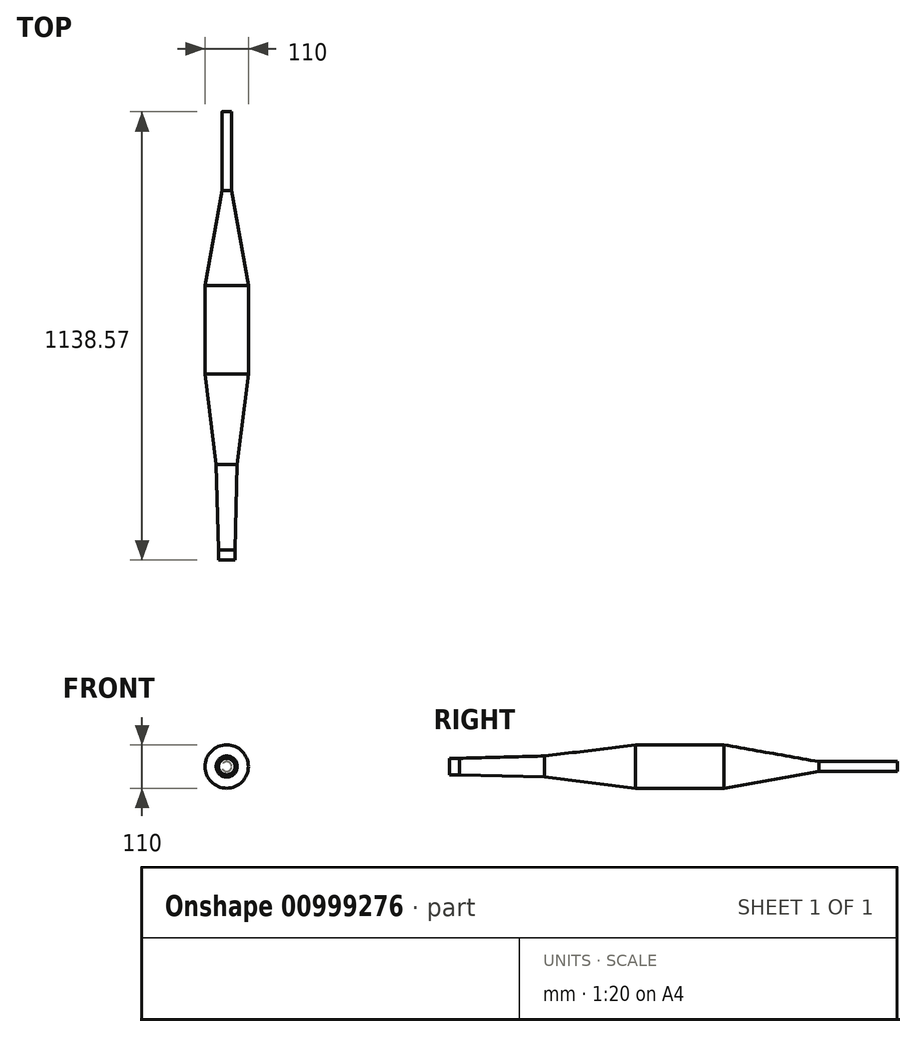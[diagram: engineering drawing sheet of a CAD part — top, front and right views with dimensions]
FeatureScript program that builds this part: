
annotation { "Feature Type Name" : "Feature", "Feature Type Description" : "" }
export const myFeature = defineFeature(function(context is Context, id is Id, definition is map)
    precondition{}
    {
        {
            var Q0;
            Q0=qCreatedBy(makeId("Right.planeOp"),FACE);
            var sketch = newSketch(context, id + "F0", { "sketchPlane" : qUnion([Q0])});
            skLineSegment(sketch, "E0", {"start": v(21.65, -12.5) * mm, "end": v(42.65, 23.87) * mm});
            skLineSegment(sketch, "E1", {"start": v(0, 191.98) * mm, "end": v(0, 233.98) * mm});
            skLineSegment(sketch, "E2", {"start": v(0, 212.98) * mm, "end": v(242, 212.98) * mm});
            skLineSegment(sketch, "E3", {"start": v(0, 212.98) * mm, "end": v(-65, 212.98) * mm});
            skLineSegment(sketch, "E4", {"start": v(242, 239.66) * mm, "end": v(242, 186.3) * mm});
            skLineSegment(sketch, "E5", {"start": v(25, 233.98) * mm, "end": v(242, 239.66) * mm});
            skLineSegment(sketch, "E6", {"start": v(25, 191.98) * mm, "end": v(242, 186.3) * mm});
            skLineSegment(sketch, "E7", {"start": v(-51.1, 50.44) * mm, "end": v(-51.1, 27.44) * mm});
            skLineSegment(sketch, "E8", {"start": v(-51.1, 38.94) * mm, "end": v(10.5, 18.19) * mm});
            skLineSegment(sketch, "E9", {"start": v(242, 212.98) * mm, "end": v(344.06, 212.98) * mm});
            skLineSegment(sketch, "E10", {"start": v(242, 239.66) * mm, "end": v(344.06, 252.2) * mm});
            skLineSegment(sketch, "E11", {"start": v(242, 186.3) * mm, "end": v(344.06, 173.76) * mm});
            skLineSegment(sketch, "E12", {"start": v(344.06, 252.2) * mm, "end": v(344.06, 173.76) * mm});
            skLineSegment(sketch, "E13", {"start": v(344.06, 212.98) * mm, "end": v(472.63, 212.98) * mm});
            skLineSegment(sketch, "E14", {"start": v(472.63, 157.98) * mm, "end": v(472.63, 267.98) * mm});
            skLineSegment(sketch, "E15", {"start": v(344.06, 252.2) * mm, "end": v(472.63, 267.98) * mm});
            skLineSegment(sketch, "E16", {"start": v(344.06, 173.76) * mm, "end": v(472.63, 157.98) * mm});
            skLineSegment(sketch, "E17", {"start": v(472.63, 212.98) * mm, "end": v(853.5, 212.98) * mm});
            skLineSegment(sketch, "E18", {"start": v(853.5, 212.98) * mm, "end": v(938.57, 212.98) * mm});
            skLineSegment(sketch, "E19", {"start": v(938.57, 200.48) * mm, "end": v(938.57, 225.48) * mm});
            skLineSegment(sketch, "E20", {"start": v(697.54, 267.98) * mm, "end": v(1009.46, 212.98) * mm, "construction": true});
            skLineSegment(sketch, "E21", {"start": v(1009.46, 212.98) * mm, "end": v(697.54, 157.98) * mm, "construction": true});
            skLineSegment(sketch, "E22", {"start": v(472.63, 267.98) * mm, "end": v(697.54, 267.98) * mm});
            skLineSegment(sketch, "E23", {"start": v(472.63, 157.98) * mm, "end": v(697.54, 157.98) * mm});
            skLineSegment(sketch, "E24", {"start": v(853.5, 185.48) * mm, "end": v(853.5, 240.48) * mm});
            skLineSegment(sketch, "E25", {"start": v(697.54, 267.98) * mm, "end": v(697.54, 157.98) * mm});
            skLineSegment(sketch, "E26", {"start": v(938.57, 225.48) * mm, "end": v(1138.57, 225.48) * mm});
            skLineSegment(sketch, "E27", {"start": v(938.57, 200.48) * mm, "end": v(1138.57, 200.48) * mm});
            skLineSegment(sketch, "E28", {"start": v(1138.57, 200.48) * mm, "end": v(1138.57, 225.48) * mm});
            skLineSegment(sketch, "E29", {"start": v(697.54, 267.98) * mm, "end": v(938.57, 225.48) * mm});
            skLineSegment(sketch, "E30", {"start": v(697.54, 157.98) * mm, "end": v(938.57, 200.48) * mm});
            skLineSegment(sketch, "E31", {"start": v(21.65, -12.5) * mm, "end": v(21.65, -190.3) * mm, "construction": true});
            skArc(sketch, "E32", {"start": v(32.15, 5.69) * mm, "mid": v(97.18, -130.66) * mm, "end": v(-6.8, -240.23) * mm, "construction": true});
            skLineSegment(sketch, "E33", {"start": v(-34.52, -109.8) * mm, "end": v(77.31, -182.43) * mm, "construction": true});
            skLineSegment(sketch, "E34", {"start": v(99.7, -196.96) * mm, "end": v(54.93, -167.9) * mm});
            skArc(sketch, "E35", {"start": v(99.7, -196.96) * mm, "mid": v(119.73, -74) * mm, "end": v(42.65, 23.87) * mm});
            skArc(sketch, "E36", {"start": v(54.93, -167.9) * mm, "mid": v(70.55, -83.29) * mm, "end": v(21.65, -12.5) * mm});
            skLineSegment(sketch, "E37", {"start": v(-6.8, -240.23) * mm, "end": v(-132.56, -266.96) * mm, "construction": true});
            skLineSegment(sketch, "E38", {"start": v(1.35, -278.6) * mm, "end": v(-14.95, -201.88) * mm});
            skLineSegment(sketch, "E39", {"start": v(-14.95, -201.88) * mm, "end": v(-144, -213.17) * mm});
            skLineSegment(sketch, "E40", {"start": v(1.35, -278.6) * mm, "end": v(-121.12, -320.76) * mm});
            skLineSegment(sketch, "E41", {"start": v(-144, -213.17) * mm, "end": v(-121.12, -320.76) * mm});
            skLineSegment(sketch, "E42", {"start": v(77.31, -182.43) * mm, "end": v(-6.8, -240.23) * mm, "construction": true});
            skArc(sketch, "E43", {"start": v(-14.95, -201.88) * mm, "mid": v(23.13, -191.34) * mm, "end": v(54.93, -167.9) * mm});
            skArc(sketch, "E44", {"start": v(1.35, -278.6) * mm, "mid": v(57.98, -246.75) * mm, "end": v(99.7, -196.96) * mm});
            skLineSegment(sketch, "E45", {"start": v(-132.56, -266.96) * mm, "end": v(-357.47, -266.96) * mm, "construction": true});
            skLineSegment(sketch, "E46", {"start": v(-368.9, -320.76) * mm, "end": v(-346.03, -213.17) * mm});
            skLineSegment(sketch, "E47", {"start": v(-368.9, -320.76) * mm, "end": v(-132.56, -266.96) * mm, "construction": true});
            skLineSegment(sketch, "E48", {"start": v(-357.47, -266.96) * mm, "end": v(-121.12, -320.76) * mm, "construction": true});
            skLineSegment(sketch, "E49", {"start": v(-346.03, -213.17) * mm, "end": v(-144, -213.17) * mm});
            skLineSegment(sketch, "E50", {"start": v(-121.12, -320.76) * mm, "end": v(-368.9, -320.76) * mm});
            skLineSegment(sketch, "E51", {"start": v(-662.57, -202.11) * mm, "end": v(-346.03, -213.17) * mm, "construction": true});
            skLineSegment(sketch, "E52", {"start": v(-662.57, -202.11) * mm, "end": v(-368.9, -320.76) * mm, "construction": true});
            skLineSegment(sketch, "E53", {"start": v(1009.46, 212.98) * mm, "end": v(697.54, 212.98) * mm, "construction": true});
            skLineSegment(sketch, "E54", {"start": v(-357.47, -266.96) * mm, "end": v(-662.57, -202.11) * mm, "construction": true});
            skLineSegment(sketch, "E55", {"start": v(-595.83, -229.08) * mm, "end": v(-590.63, -204.62) * mm});
            skLineSegment(sketch, "E56", {"start": v(-590.63, -204.62) * mm, "end": v(-786.26, -163.04) * mm});
            skLineSegment(sketch, "E57", {"start": v(-786.26, -163.04) * mm, "end": v(-791.46, -187.5) * mm});
            skLineSegment(sketch, "E58", {"start": v(-791.46, -187.5) * mm, "end": v(-595.83, -229.08) * mm});
            skLineSegment(sketch, "E59", {"start": v(-590.63, -204.62) * mm, "end": v(-346.03, -213.17) * mm});
            skLineSegment(sketch, "E60", {"start": v(-595.83, -229.08) * mm, "end": v(-368.9, -320.76) * mm});
            skLineSegment(sketch, "E61", {"start": v(42.65, 23.87) * mm, "end": v(21, 36.37) * mm});
            skLineSegment(sketch, "E62", {"start": v(21, 36.37) * mm, "end": v(0, 0) * mm});
            skLineSegment(sketch, "E63", {"start": v(0, 0) * mm, "end": v(21.65, -12.5) * mm});
            skLineSegment(sketch, "E64", {"start": v(0, 212.98) * mm, "end": v(25, 212.98) * mm});
            skLineSegment(sketch, "E65", {"start": v(25, 233.98) * mm, "end": v(25, 191.98) * mm});
            skLineSegment(sketch, "E66", {"start": v(0, 233.98) * mm, "end": v(25, 233.98) * mm});
            skLineSegment(sketch, "E67", {"start": v(0, 191.98) * mm, "end": v(25, 191.98) * mm});
            skLineSegment(sketch, "E68", {"start": v(-51.1, 27.44) * mm, "end": v(0, 0) * mm});
            skLineSegment(sketch, "E69", {"start": v(-51.1, 50.44) * mm, "end": v(21, 36.37) * mm});
            skLineSegment(sketch, "E70", {"start": v(10.5, 18.19) * mm, "end": v(32.15, 5.69) * mm});
            skLineSegment(sketch, "E71", {"start": v(938.57, 212.98) * mm, "end": v(1138.57, 212.98) * mm});
            skSolve(sketch);
        }
        {
            var Q0;
            {var subQ2=sQuery(id+"F0.wireOp",EDGE,"E64");Q0=makeQuery(id+"F0.imprint","IMPRINT",FACE,{"disambiguationData":[TD([[makeQuery(id+"F0.imprint","IMPRINT",EDGE,{"derivedFrom":subQ2}),1.0]])]});}
            var Q1;
            {var subQ0=sQuery(id+"F0.wireOp",EDGE,"E2");Q1=makeQuery(id+"F0.imprint","IMPRINT",FACE,{"disambiguationData":[TD([[makeQuery(id+"F0.imprint","IMPRINT",EDGE,{"derivedFrom":subQ0}),1.0]])]});}
            var Q2;
            {var subQ0=sQuery(id+"F0.wireOp",EDGE,"E9");Q2=makeQuery(id+"F0.imprint","IMPRINT",FACE,{"disambiguationData":[TD([[makeQuery(id+"F0.imprint","IMPRINT",EDGE,{"derivedFrom":subQ0}),1.0]])]});}
            var Q3;
            {var subQ0=sQuery(id+"F0.wireOp",EDGE,"E13");Q3=makeQuery(id+"F0.imprint","IMPRINT",FACE,{"disambiguationData":[TD([[makeQuery(id+"F0.imprint","IMPRINT",EDGE,{"derivedFrom":subQ0}),1.0]])]});}
            var Q4;
            {var subQ3=sQuery(id+"F0.wireOp",EDGE,"E22");Q4=makeQuery(id+"F0.imprint","IMPRINT",FACE,{"disambiguationData":[TD([[makeQuery(id+"F0.imprint","IMPRINT",EDGE,{"derivedFrom":subQ3}),-1.0]])]});}
            var Q5;
            {var subQ1=sQuery(id+"F0.wireOp",EDGE,"E17");var subQ3=sQuery(id+"F0.wireOp",EDGE,"E25");var subQ4=makeQuery(id+"F0.imprint","INTERSECT",VERTEX,{"derivedFrom":[subQ1,subQ3]});Q5=makeQuery(id+"F0.imprint","IMPRINT",FACE,{"disambiguationData":[TD([[makeQuery(id+"F0.imprint","IMPRINT",EDGE,{"disambiguationData":[TD([[subQ4,-1.0]])],"derivedFrom":subQ1}),1.0]])]});}
            var Q6;
            {var subQ0=sQuery(id+"F0.wireOp",EDGE,"E18");Q6=makeQuery(id+"F0.imprint","IMPRINT",FACE,{"disambiguationData":[TD([[makeQuery(id+"F0.imprint","IMPRINT",EDGE,{"derivedFrom":subQ0}),1.0]])]});}
            var Q7;
            {var subQ2=sQuery(id+"F0.wireOp",EDGE,"E26");Q7=makeQuery(id+"F0.imprint","IMPRINT",FACE,{"disambiguationData":[TD([[makeQuery(id+"F0.imprint","IMPRINT",EDGE,{"derivedFrom":subQ2}),-1.0]])]});}
            var Q8;
            Q8=sQuery(id+"F0.wireOp",EDGE,"E3");
            revolve(context, id + "F1", {"surfaceOperationType" : NewSurfaceOperationType.NEW, "entities" : qUnion([Q0, Q1, Q2, Q3, Q4, Q5, Q6, Q7]), "axis" : qUnion([Q8]), "revolveType" : RevolveType.FULL});
        }
        {
            var Q0;
            {var subQ0=sQuery(id+"F0.wireOp",EDGE,"E61");Q0=makeQuery(id+"F0.imprint","IMPRINT",FACE,{"disambiguationData":[TD([[makeQuery(id+"F0.imprint","IMPRINT",EDGE,{"derivedFrom":subQ0}),1.0]])]});}
            var Q1;
            Q1=sQuery(id+"F0.wireOp",EDGE,"E61");
            var Q2;
            Q2=sQuery(id+"F0.wireOp",EDGE,"E70");
            revolve(context, id + "F2", {"bodyType" : ToolBodyType.SURFACE, "surfaceOperationType" : NewSurfaceOperationType.NEW, "entities" : qUnion([Q0]), "surfaceEntities" : qUnion([Q1]), "axis" : qUnion([Q2]), "revolveType" : RevolveType.FULL});
        }
        {
            var Q0;
            Q0=sQuery(id+"F0.wireOp",EDGE,"E34");
            var Q1;
            {var subQ0=sQuery(id+"F0.wireOp",EDGE,"E36");Q1=makeQuery(id+"F0.imprint","IMPRINT",FACE,{"disambiguationData":[TD([[makeQuery(id+"F0.imprint","IMPRINT",EDGE,{"derivedFrom":subQ0}),-1.0]])]});}
            cPlane(context, id + "F3", {"entities" : qUnion([Q0, Q1]), "cplaneType" : CPlaneType.LINE_ANGLE, "offset" : 0 * mm, "angle" : 90 * degree, "width" : 152.4 * mm, "height" : 152.4 * mm});
        }
        {
            var Q0;
            Q0=qCreatedBy(id+"F3.planeOp",FACE);
            var sketch = newSketch(context, id + "F4", { "sketchPlane" : qUnion([Q0])});
            skCircle(sketch, "E72", {"center": v(0, -164.2) * mm, "radius": 26.68 * mm});
            skSolve(sketch);
        }
        {
            var Q0;
            Q0=makeQuery(id+"F4.imprint","IMPRINT",FACE,{"disambiguationData":[TD([[makeQuery(id+"F4.imprint","IMPRINT",EDGE,{"derivedFrom":sQuery(id+"F4.wireOp",EDGE,"E72")}),1.0]])]});
            var Q1;
            Q1=makeQuery(id+"F2.opRevolve","SWEPT_BODY",BODY,{"disambiguationData":[OSD([sQuery(id+"F0.wireOp",EDGE,"E61")])]});
            var Q2;
            Q2=makeQuery(id+"F2.opRevolve","SWEPT_EDGE",EDGE,{"disambiguationData":[OSD([sQuery(id+"F0.wireOp",VERTEX,"E61.start")])]});
            var Q3;
            Q3=sQuery(id+"F4.wireOp",EDGE,"E72");
            var Q4;
            Q4=sQuery(id+"F0.wireOp",EDGE,"E35");
            var Q5;
            Q5=sQuery(id+"F0.wireOp",EDGE,"E36");
            loft(context, id + "F5", {"bodyType" : ToolBodyType.SURFACE, "operationType" : NewBodyOperationType.ADD, "surfaceOperationType" : NewSurfaceOperationType.ADD, "addGuides" : true, "sheetProfilesArray" : [{ "sheetProfileEntities" : qUnion([Q0]) }, { "sheetProfileEntities" : qUnion([Q1]) }], "wireProfilesArray" : [{ "wireProfileEntities" : qUnion([Q2]) }, { "wireProfileEntities" : qUnion([Q3]) }], "guidesArray" : [{ "guideEntities" : qUnion([Q4]), "guideDerivativeType" : LoftGuideDerivativeType.DEFAULT, "guideDerivativeMagnitude" : 1 }, { "guideEntities" : qUnion([Q5]), "guideDerivativeType" : LoftGuideDerivativeType.DEFAULT, "guideDerivativeMagnitude" : 1 }]});
        }
        {
            var Q0;
            Q0=sQuery(id+"F0.wireOp",EDGE,"E38");
            var Q1;
            {var subQ5=sQuery(id+"F0.wireOp",EDGE,"E43");Q1=makeQuery(id+"F0.imprint","IMPRINT",FACE,{"disambiguationData":[TD([[makeQuery(id+"F0.imprint","IMPRINT",EDGE,{"derivedFrom":subQ5}),-1.0]])]});}
            cPlane(context, id + "F6", {"entities" : qUnion([Q0, Q1]), "cplaneType" : CPlaneType.LINE_ANGLE, "offset" : 25.4 * mm, "angle" : 93 * degree, "width" : 152.4 * mm, "height" : 152.4 * mm});
        }
        {
            var Q0;
            Q0=qCreatedBy(id+"F6.planeOp",FACE);
            var sketch = newSketch(context, id + "F7", { "sketchPlane" : qUnion([Q0])});
            skCircle(sketch, "E73", {"center": v(-2.96, -233.57) * mm, "radius": 39.21 * mm});
            skSolve(sketch);
        }
        {
            var Q1;
            Q1=makeQuery(id+"F5.opLoft","CAP_FACE",FACE,{"disambiguationData":[OSD([makeQuery(id+"F4.imprint","IMPRINT",FACE,{"disambiguationData":[TD([[makeQuery(id+"F4.imprint","IMPRINT",EDGE,{"derivedFrom":sQuery(id+"F4.wireOp",EDGE,"E72")}),1.0]])]})])],"isStart":true});
            var Q2;
            Q2=makeQuery(id+"F7.imprint","IMPRINT",FACE,{"disambiguationData":[TD([[makeQuery(id+"F7.imprint","IMPRINT",EDGE,{"derivedFrom":sQuery(id+"F7.wireOp",EDGE,"E73")}),1.0]])]});
            var Q3;
            Q3=sQuery(id+"F7.wireOp",EDGE,"E73");
            var Q4;
            Q4=makeQuery(id+"F4.imprint","IMPRINT",FACE,{"disambiguationData":[TD([[makeQuery(id+"F4.imprint","IMPRINT",EDGE,{"derivedFrom":sQuery(id+"F4.wireOp",EDGE,"E72")}),1.0]])]});
            var Q5;
            Q5=sQuery(id+"F0.wireOp",EDGE,"E44");
            var Q6;
            Q6=sQuery(id+"F0.wireOp",EDGE,"E43");
            loft(context, id + "F8", {"bodyType" : ToolBodyType.SURFACE, "operationType" : NewBodyOperationType.ADD, "addGuides" : true, "sheetProfilesArray" : [{ "sheetProfileEntities" : qUnion([Q1]) }, { "sheetProfileEntities" : qUnion([Q2]) }], "wireProfilesArray" : [{ "wireProfileEntities" : qUnion([Q3]) }, { "wireProfileEntities" : qUnion([Q4]) }], "guidesArray" : [{ "guideEntities" : qUnion([Q5]), "guideDerivativeType" : LoftGuideDerivativeType.DEFAULT, "guideDerivativeMagnitude" : 1 }, { "guideEntities" : qUnion([Q6]), "guideDerivativeType" : LoftGuideDerivativeType.DEFAULT, "guideDerivativeMagnitude" : 1 }]});
        }
        {
            var Q0;
            Q0=sQuery(id+"F0.wireOp",EDGE,"E41");
            var Q1;
            {var subQ0=sQuery(id+"F0.wireOp",EDGE,"E37");Q1=makeQuery(id+"F0.imprint","IMPRINT",FACE,{"disambiguationData":[TD([[makeQuery(id+"F0.imprint","IMPRINT",EDGE,{"derivedFrom":subQ0}),-1.0]])]});}
            cPlane(context, id + "F9", {"entities" : qUnion([Q0, Q1]), "cplaneType" : CPlaneType.LINE_ANGLE, "offset" : 25.4 * mm, "angle" : 97 * degree, "oppositeDirection" : true, "width" : 152.4 * mm, "height" : 152.4 * mm});
        }
        {
            var Q0;
            Q0=qCreatedBy(id+"F9.planeOp",FACE);
            var sketch = newSketch(context, id + "F10", { "sketchPlane" : qUnion([Q0])});
            skCircle(sketch, "E74", {"center": v(-22.57, -233.57) * mm, "radius": 55 * mm, "construction": true});
            skCircle(sketch, "E75", {"center": v(-16.22, -233.57) * mm, "radius": 55 * mm});
            skLineSegment(sketch, "E76", {"start": v(-16.22, -233.57) * mm, "end": v(-22.57, -233.57) * mm});
            skSolve(sketch);
        }
        {
            var Q1;
            Q1=makeQuery(id+"F8.opLoft","CAP_FACE",FACE,{"disambiguationData":[OSD([makeQuery(id+"F7.imprint","IMPRINT",FACE,{"disambiguationData":[TD([[makeQuery(id+"F7.imprint","IMPRINT",EDGE,{"derivedFrom":sQuery(id+"F7.wireOp",EDGE,"E73")}),1.0]])]})])],"isStart":true});
            var Q2;
            Q2=makeQuery(id+"F10.imprint","IMPRINT",FACE,{"disambiguationData":[TD([[makeQuery(id+"F10.imprint","IMPRINT",EDGE,{"derivedFrom":sQuery(id+"F10.wireOp",EDGE,"E74")}),1.0]])]});
            var Q3;
            Q3=sQuery(id+"F7.wireOp",EDGE,"E73");
            var Q4;
            Q4=sQuery(id+"F10.wireOp",EDGE,"E75");
            loft(context, id + "F11", {"bodyType" : ToolBodyType.SURFACE, "surfaceOperationType" : NewSurfaceOperationType.ADD, "sheetProfilesArray" : [{ "sheetProfileEntities" : qUnion([Q1]) }, { "sheetProfileEntities" : qUnion([Q2]) }], "wireProfilesArray" : [{ "wireProfileEntities" : qUnion([Q3]) }, { "wireProfileEntities" : qUnion([Q4]) }]});
        }
        {
            var Q0;
            Q0=sQuery(id+"F0.wireOp",EDGE,"E46");
            var Q1;
            {var subQ0=sQuery(id+"F0.wireOp",EDGE,"E45");Q1=makeQuery(id+"F0.imprint","IMPRINT",FACE,{"disambiguationData":[TD([[makeQuery(id+"F0.imprint","IMPRINT",EDGE,{"derivedFrom":subQ0}),-1.0]])]});}
            cPlane(context, id + "F12", {"entities" : qUnion([Q0, Q1]), "cplaneType" : CPlaneType.LINE_ANGLE, "offset" : 25.4 * mm, "angle" : 115 * degree, "width" : 152.4 * mm, "height" : 152.4 * mm});
        }
        {
            var Q0;
            Q0=qCreatedBy(id+"F12.planeOp",FACE);
            var sketch = newSketch(context, id + "F13", { "sketchPlane" : qUnion([Q0])});
            skCircle(sketch, "E77", {"center": v(124.31, -335.45) * mm, "radius": 55 * mm, "construction": true});
            skLineSegment(sketch, "E78", {"start": v(124.31, -335.45) * mm, "end": v(105.26, -335.45) * mm, "construction": true});
            skCircle(sketch, "E79", {"center": v(105.26, -335.45) * mm, "radius": 55 * mm});
            skLineSegment(sketch, "E80", {"start": v(105.26, -390.45) * mm, "end": v(105.26, -280.45) * mm, "construction": true});
            skSolve(sketch);
        }
        {
            var Q0;
            Q0=sQuery(id+"F13.wireOp",VERTEX,"E80.end");
            var Q1;
            Q1=sQuery(id+"F13.wireOp",VERTEX,"E80.start");
            var Q2;
            Q2=sQuery(id+"F10.wireOp",VERTEX,"E76.start");
            cPlane(context, id + "F14", {"entities" : qUnion([Q0, Q1, Q2]), "cplaneType" : CPlaneType.THREE_POINT, "offset" : 25.4 * mm, "width" : 152.4 * mm, "height" : 152.4 * mm});
        }
        {
            var Q0;
            Q0=qCreatedBy(id+"F14.planeOp",FACE);
            var sketch = newSketch(context, id + "F15", { "sketchPlane" : qUnion([Q0])});
            skLineSegment(sketch, "E81", {"start": v(338.71, -214.64) * mm, "end": v(143.4, -212.9) * mm});
            skLineSegment(sketch, "E82", {"start": v(361.61, -322.23) * mm, "end": v(120.78, -320.55) * mm});
            skSolve(sketch);
        }
        {
            var Q0;
            Q0=makeQuery(id+"F11.opLoft","CAP_FACE",FACE,{"disambiguationData":[OSD([makeQuery(id+"F10.imprint","IMPRINT",FACE,{"disambiguationData":[TD([[makeQuery(id+"F10.imprint","IMPRINT",EDGE,{"derivedFrom":sQuery(id+"F10.wireOp",EDGE,"E74")}),1.0]])]})])],"isStart":true});
            var Q1;
            Q1=makeQuery(id+"F13.imprint","IMPRINT",FACE,{"disambiguationData":[TD([[makeQuery(id+"F13.imprint","IMPRINT",EDGE,{"derivedFrom":sQuery(id+"F13.wireOp",EDGE,"E77")}),1.0]])]});
            var Q2;
            Q2=sQuery(id+"F13.wireOp",EDGE,"E79");
            var Q3;
            Q3=sQuery(id+"F10.wireOp",EDGE,"E75");
            var Q4;
            Q4=sQuery(id+"F15.wireOp",EDGE,"E81");
            var Q5;
            Q5=sQuery(id+"F15.wireOp",EDGE,"E82");
            loft(context, id + "F16", {"bodyType" : ToolBodyType.SURFACE, "surfaceOperationType" : NewSurfaceOperationType.ADD, "addGuides" : true, "sheetProfilesArray" : [{ "sheetProfileEntities" : qUnion([Q0]) }, { "sheetProfileEntities" : qUnion([Q1]) }], "wireProfilesArray" : [{ "wireProfileEntities" : qUnion([Q2]) }, { "wireProfileEntities" : qUnion([Q3]) }], "guidesArray" : [{ "guideEntities" : qUnion([Q4]), "guideDerivativeType" : LoftGuideDerivativeType.DEFAULT, "guideDerivativeMagnitude" : 1 }, { "guideEntities" : qUnion([Q5]), "guideDerivativeType" : LoftGuideDerivativeType.DEFAULT, "guideDerivativeMagnitude" : 1 }]});
        }
        {
            var Q0;
            Q0=sQuery(id+"F0.wireOp",EDGE,"E55");
            cPlane(context, id + "F17", {"entities" : qUnion([Q0]), "cplaneType" : CPlaneType.LINE_ANGLE, "offset" : 25.4 * mm, "angle" : 70 * degree, "oppositeDirection" : true, "width" : 152.4 * mm, "height" : 152.4 * mm});
        }
        {
            var Q0;
            Q0=qCreatedBy(id+"F17.planeOp",FACE);
            var sketch = newSketch(context, id + "F18", { "sketchPlane" : qUnion([Q0])});
            skCircle(sketch, "E83", {"center": v(-183.04, -335.45) * mm, "radius": 12.5 * mm, "construction": true});
            skLineSegment(sketch, "E84", {"start": v(-183.04, -335.45) * mm, "end": v(-5.24, -335.45) * mm, "construction": true});
            skCircle(sketch, "E85", {"center": v(-5.24, -297.35) * mm, "radius": 12.5 * mm});
            skLineSegment(sketch, "E86", {"start": v(-5.24, -335.45) * mm, "end": v(-5.24, -297.35) * mm});
            skSolve(sketch);
        }
        {
            var Q1;
            Q1=makeQuery(id+"F16.opLoft","CAP_FACE",FACE,{"disambiguationData":[OSD([makeQuery(id+"F13.imprint","IMPRINT",FACE,{"disambiguationData":[TD([[makeQuery(id+"F13.imprint","IMPRINT",EDGE,{"derivedFrom":sQuery(id+"F13.wireOp",EDGE,"E77")}),1.0]])]})])],"isStart":true});
            var Q2;
            Q2=makeQuery(id+"F18.imprint","IMPRINT",FACE,{"disambiguationData":[TD([[makeQuery(id+"F18.imprint","IMPRINT",EDGE,{"derivedFrom":sQuery(id+"F18.wireOp",EDGE,"E83")}),1.0]])]});
            var Q3;
            Q3=sQuery(id+"F18.wireOp",EDGE,"E85");
            var Q4;
            Q4=sQuery(id+"F13.wireOp",EDGE,"E79");
            loft(context, id + "F19", {"bodyType" : ToolBodyType.SURFACE, "surfaceOperationType" : NewSurfaceOperationType.ADD, "sheetProfilesArray" : [{ "sheetProfileEntities" : qUnion([Q1]) }, { "sheetProfileEntities" : qUnion([Q2]) }], "wireProfilesArray" : [{ "wireProfileEntities" : qUnion([Q3]) }, { "wireProfileEntities" : qUnion([Q4]) }]});
        }
        {
            var Q0;
            Q0=makeQuery(id+"F18.imprint","IMPRINT",FACE,{"disambiguationData":[TD([[makeQuery(id+"F18.imprint","IMPRINT",EDGE,{"derivedFrom":sQuery(id+"F18.wireOp",EDGE,"E85")}),1.0]])]});
            var Q1;
            Q1=sQuery(id+"F18.wireOp",EDGE,"E85");
            extrude(context, id + "F20", {"entities" : qUnion([Q0]), "bodyType" : ToolBodyType.SURFACE, "surfaceOperationType" : NewSurfaceOperationType.ADD, "surfaceEntities" : qUnion([Q1]), "depth" : 120 * mm, "offsetDistance" : 25.4 * mm});
        }
        {
            var Q0;
            Q0=sQuery(id+"F0.wireOp",EDGE,"E57");
            cPlane(context, id + "F21", {"entities" : qUnion([Q0]), "cplaneType" : CPlaneType.LINE_ANGLE, "offset" : 25.4 * mm, "angle" : 90 * degree, "oppositeDirection" : true, "width" : 152.4 * mm, "height" : 152.4 * mm});
        }
        {
            var Q0;
            Q0=qCreatedBy(id+"F21.planeOp",FACE);
            var sketch = newSketch(context, id + "F22", { "sketchPlane" : qUnion([Q0])});
            skLineSegment(sketch, "E87", {"start": v(209.55, -306.88) * mm, "end": v(209.55, -281.88) * mm, "construction": true});
            skCircle(sketch, "E88", {"center": v(209.55, -294.38) * mm, "radius": 12.5 * mm});
            skLineSegment(sketch, "E89", {"start": v(0, -335.45) * mm, "end": v(209.55, -335.45) * mm, "construction": true});
            skLineSegment(sketch, "E90", {"start": v(209.55, -306.88) * mm, "end": v(209.55, -335.45) * mm, "construction": true});
            skSolve(sketch);
        }
        {
            var Q0;
            Q0=makeQuery(id+"F20.opExtrude","CAP_EDGE",EDGE,{"disambiguationData":[OSD([sQuery(id+"F18.wireOp",EDGE,"E85")])],"isStart":false});
            var Q1;
            Q1=sQuery(id+"F22.wireOp",VERTEX,"E88.center");
            cPlane(context, id + "F23", {"entities" : qUnion([Q0, Q1]), "cplaneType" : CPlaneType.CURVE_POINT, "offset" : 25.4 * mm, "width" : 152.4 * mm, "height" : 152.4 * mm});
        }
        {
            var Q0;
            Q0=qCreatedBy(id+"F23.planeOp",FACE);
            var sketch = newSketch(context, id + "F24", { "sketchPlane" : qUnion([Q0])});
            skLineSegment(sketch, "E91", {"start": v(226.73, 728.95) * mm, "end": v(225.3, 580.87) * mm});
            skLineSegment(sketch, "E92", {"start": v(213.56, 585.15) * mm, "end": v(237.05, 576.59) * mm, "construction": true});
            skSolve(sketch);
        }
    });
